# Revit family: BE_84463_de_DE
name_source: partatom
category: Lighting Fixtures
revit_build: Autodesk Revit 2017 (Build: 20160225_1515(x64)
units: mm (PartAtom-declared; Revit-internal decimal feet)

## family parameters
Cut with Voids When Loaded = Yes
Host = Face
Light Source = Yes
Part Type = Normal
Room Calculation Point = Yes
Round Connector Dimension = Use Diameter
Shared = No

## types (4) — shared parameters
AC/DC = AC/DC
Aktualisierung = 2021-02-26T04:00:16
Apparent Load = 0 VA
BEGA_Dummy = No
BEGA_IES = Yes
BEGA_Intern = Yes
BEGA_Intern_Konstruktion = Yes
BEGA_Intern_an = Yes
BEGA_Intern_aus = Yes
Beschreibung_Sonderanfertigung = Hier können Sie Informationen zur Sonderanfertigung eintragen.
CE_Konformität = ja
Color Filter = 16777215
Description = Pollerleuchte
Dimming Lamp Color Temperature Shift = <None>
ENEC = ja
Energieeffizienzklasse = LED A++ - A
Farbwiedergabeindex = CRI > 80
Frequenz = 0/50-60 Hz
Gewicht = 12.3 kg
Lamp = LED 11.5 W
Lastklassifizierung = Beleuchtung
Lebensdauerkriterien = L70B50 @ 25 °C = 200000 h
Logo = BEGA_Logo.png
M_W = No
Manufacturer = BEGA
Material_02 = BEGA_Oberfläche_Silber_matt
Material_09 = BEGA_Glas_klar
Material_15 = BEGA_Leuchtmedium_matt
Material_17 = BEGA_Reflektor
Produktdatenblatt = http://www.bega.de
Schutzart = IP 65
Schutzklasse = I
Sonderanfertigung = No
Spannung = 240 V
Tilt Angle = 0.00°
Type Image = 84463.png
URL = https://www.bega.com
Umgebungstemperatur = 25 °C
zero-valued in all types: Default Elevation

## per-type parameters (varying)
| type | Bestellnummer | Farbtemperatur | LED_Modulbezeichnung | Lampenlichtstrom | Leuchtenlichtstrom | M_A | M_G | Model | Photometric Web File |
| BEGA_84463_Grafit_K4 | 84463K4 | 4000 K | LED-1066/840 | 2340 lm | 1893 lm | No | Yes | 84463K4 | BE_84463K4.IES |
| BEGA_84463_Silber_K3 | 84463AK3 | 3000 K | LED-1066/830 | 2275 lm | 1840 lm | Yes | No | 84463AK3 | BE_84463K3.IES |
| BEGA_84463_Grafit_K3 | 84463K3 | 3000 K | LED-1066/830 | 2275 lm | 1840 lm | No | Yes | 84463K3 | BE_84463K3.IES |
| BEGA_84463_Silber_K4 | 84463AK4 | 4000 K | LED-1066/840 | 2340 lm | 1893 lm | Yes | No | 84463AK4 | BE_84463K4.IES |
